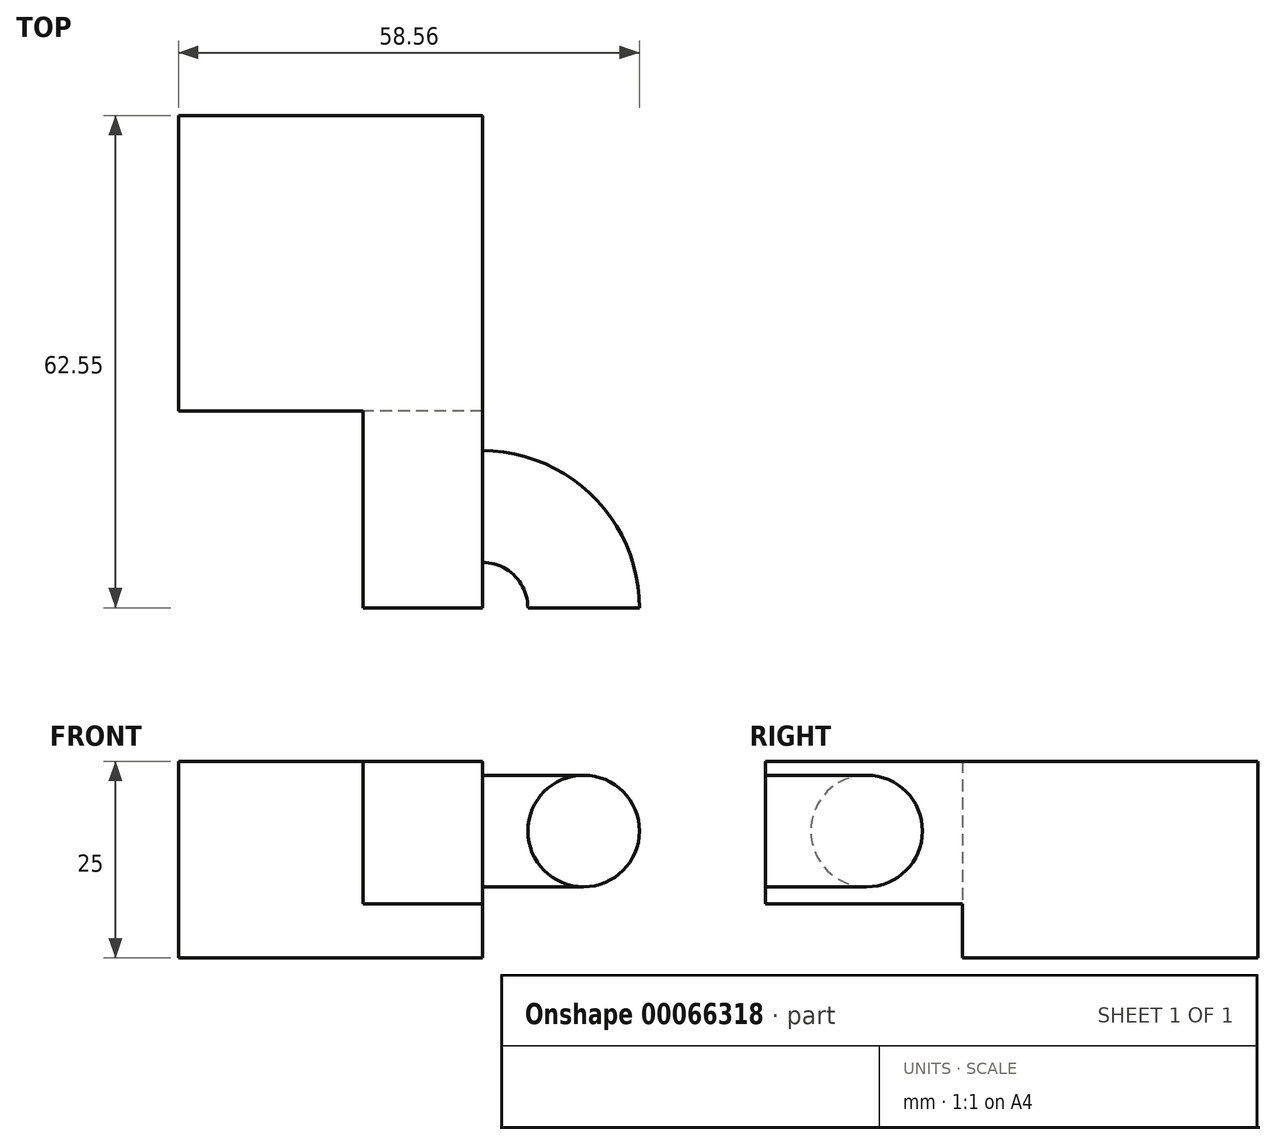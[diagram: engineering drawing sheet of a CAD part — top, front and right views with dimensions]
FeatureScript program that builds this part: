
annotation { "Feature Type Name" : "Feature", "Feature Type Description" : "" }
export const myFeature = defineFeature(function(context is Context, id is Id, definition is map)
    precondition{}
    {
        {
            var Q0;
            Q0=qCreatedBy(makeId("Top.planeOp"),FACE);
            var sketch = newSketch(context, id + "F0", { "sketchPlane" : qUnion([Q0])});
            skLineSegment(sketch, "E0.bottom", {"start": v(0, 0) * mm, "end": v(-38.61, 0) * mm});
            skLineSegment(sketch, "E0.top", {"start": v(0, 37.55) * mm, "end": v(-38.61, 37.55) * mm});
            skLineSegment(sketch, "E0.left", {"start": v(0, 0) * mm, "end": v(0, 37.55) * mm});
            skLineSegment(sketch, "E0.right", {"start": v(-38.61, 0) * mm, "end": v(-38.61, 37.55) * mm});
            skSolve(sketch);
        }
        {
            var Q0;
            Q0 = qSketchRegion(id + "F0", true);
            extrude(context, id + "F1", {"entities" : qUnion([Q0]), "depth" : 25 * mm});
        }
        {
            var Q0;
            Q0=makeQuery(id+"F1.opExtrude","SWEPT_FACE",FACE,{"disambiguationData":[OSD([sQuery(id+"F0.wireOp",EDGE,"E0.bottom")])]});
            var sketch = newSketch(context, id + "F2", { "sketchPlane" : qUnion([Q0])});
            skLineSegment(sketch, "E1.bottom", {"start": v(0, 25) * mm, "end": v(-15.18, 25) * mm});
            skLineSegment(sketch, "E1.top", {"start": v(0, 6.86) * mm, "end": v(-15.18, 6.86) * mm});
            skLineSegment(sketch, "E1.left", {"start": v(0, 25) * mm, "end": v(0, 6.86) * mm});
            skLineSegment(sketch, "E1.right", {"start": v(-15.18, 25) * mm, "end": v(-15.18, 6.86) * mm});
            skSolve(sketch);
        }
        {
            var Q0;
            Q0 = qSketchRegion(id + "F2", true);
            extrude(context, id + "F3", {"entities" : qUnion([Q0]), "operationType" : NewBodyOperationType.ADD, "depth" : 25 * mm});
        }
        {
            var Q0;
            Q0=makeQuery(id+"F3.boolean.opBoolean","MERGE",FACE,{"derivedFrom":[makeQuery(id+"F1.opExtrude","SWEPT_FACE",FACE,{"disambiguationData":[OSD([sQuery(id+"F0.wireOp",EDGE,"E0.left")])]}),makeQuery(id+"F3.opExtrude","SWEPT_FACE",FACE,{"disambiguationData":[OSD([sQuery(id+"F2.wireOp",EDGE,"E1.left")])]})]});
            var sketch = newSketch(context, id + "F4", { "sketchPlane" : qUnion([Q0])});
            skCircle(sketch, "E2", {"center": v(-12.14, 16.14) * mm, "radius": 7.09 * mm});
            skSolve(sketch);
        }
        {
            var Q0;
            Q0=makeQuery(id+"F4.imprint","IMPRINT",FACE,{"disambiguationData":[TD([[makeQuery(id+"F4.imprint","IMPRINT",EDGE,{"derivedFrom":sQuery(id+"F4.wireOp",EDGE,"E2")}),1.0]])]});
            var Q1;
            Q1=makeQuery(id+"F3.opExtrude","CAP_EDGE",EDGE,{"disambiguationData":[OSD([sQuery(id+"F2.wireOp",EDGE,"E1.left")])],"isStart":false});
            revolve(context, id + "F5", {"operationType" : NewBodyOperationType.ADD, "entities" : qUnion([Q0]), "axis" : qUnion([Q1]), "revolveType" : RevolveType.ONE_DIRECTION, "angle" : 90 * degree});
        }
    });
